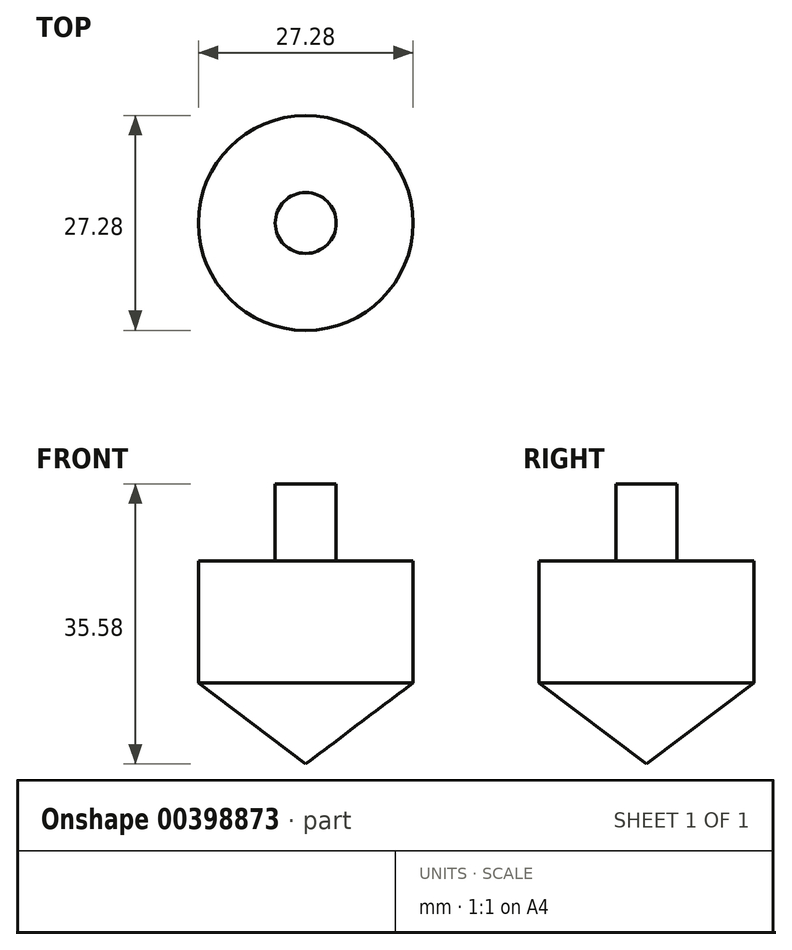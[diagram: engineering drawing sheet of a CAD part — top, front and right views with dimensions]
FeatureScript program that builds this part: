
annotation { "Feature Type Name" : "Feature", "Feature Type Description" : "" }
export const myFeature = defineFeature(function(context is Context, id is Id, definition is map)
    precondition{}
    {
        {
            var Q0;
            Q0=qCreatedBy(makeId("Front.planeOp"),FACE);
            var sketch = newSketch(context, id + "F0", { "sketchPlane" : qUnion([Q0])});
            skLineSegment(sketch, "E0", {"start": v(0, 9.59) * mm, "end": v(0, 45.17) * mm});
            skLineSegment(sketch, "E1", {"start": v(0, 45.17) * mm, "end": v(3.87, 45.17) * mm});
            skLineSegment(sketch, "E2", {"start": v(3.87, 45.17) * mm, "end": v(3.87, 35.4) * mm});
            skLineSegment(sketch, "E3", {"start": v(3.87, 35.4) * mm, "end": v(13.64, 35.4) * mm});
            skLineSegment(sketch, "E4", {"start": v(13.64, 35.4) * mm, "end": v(13.64, 19.91) * mm});
            skLineSegment(sketch, "E5", {"start": v(13.64, 19.91) * mm, "end": v(0, 9.59) * mm});
            skSolve(sketch);
        }
        {
            var Q0;
            Q0 = qSketchRegion(id + "F0", true);
            var Q1;
            Q1=sQuery(id+"F0.wireOp",EDGE,"E0");
            revolve(context, id + "F1", {"entities" : qUnion([Q0]), "axis" : qUnion([Q1]), "revolveType" : RevolveType.FULL});
        }
    });
